# Revit family: TL_2D_Gaplok_GRD-10
name_source: partatom
category: Detail Items
revit_build: Autodesk Revit 2016 (Build: 20150714_1515(x64)
units: mm (PartAtom-declared; Revit-internal decimal feet)

## family parameters
Rotate with component = No
Shared = No

## types (8) — shared parameters

## per-type parameters (varying)
| type | Gridlok-Rail End | Gridlok-Rail Side | Gridlok-Top 90 Bracket | Gridlok-Top Bracket End |
| Gridlok-Plan | No | No | No | No |
| Gridlok-Side | No | No | No | No |
| Gridlok-End | No | No | No | No |
| Gridlok-Rail_Side | No | Yes | No | No |
| Gridlok-Rail_End | Yes | No | No | No |
| Gridlok-Top 90 Side | No | No | Yes | No |
| Gridlok-Top 45 Side | No | No | No | No |
| Gridlok-Top End | No | No | No | Yes |

type visibility flags (boolean, named after types; folded from table):
- Gridlok-Plan: Yes: Gridlok-Plan
- Gridlok-Side: Yes: Gridlok-Side
- Gridlok-End: Yes: Gridlok-End
- Gridlok-Rail_Side: Yes: (none)
- Gridlok-Rail_End: Yes: (none)
- Gridlok-Top 90 Side: Yes: (none)
- Gridlok-Top 45 Side: Yes: Gridlok-Top 45 Side
- Gridlok-Top End: Yes: (none)

## geometry (parser evidence)
native form markers: Sweep x1
no freeform markers — native parametric forms only
